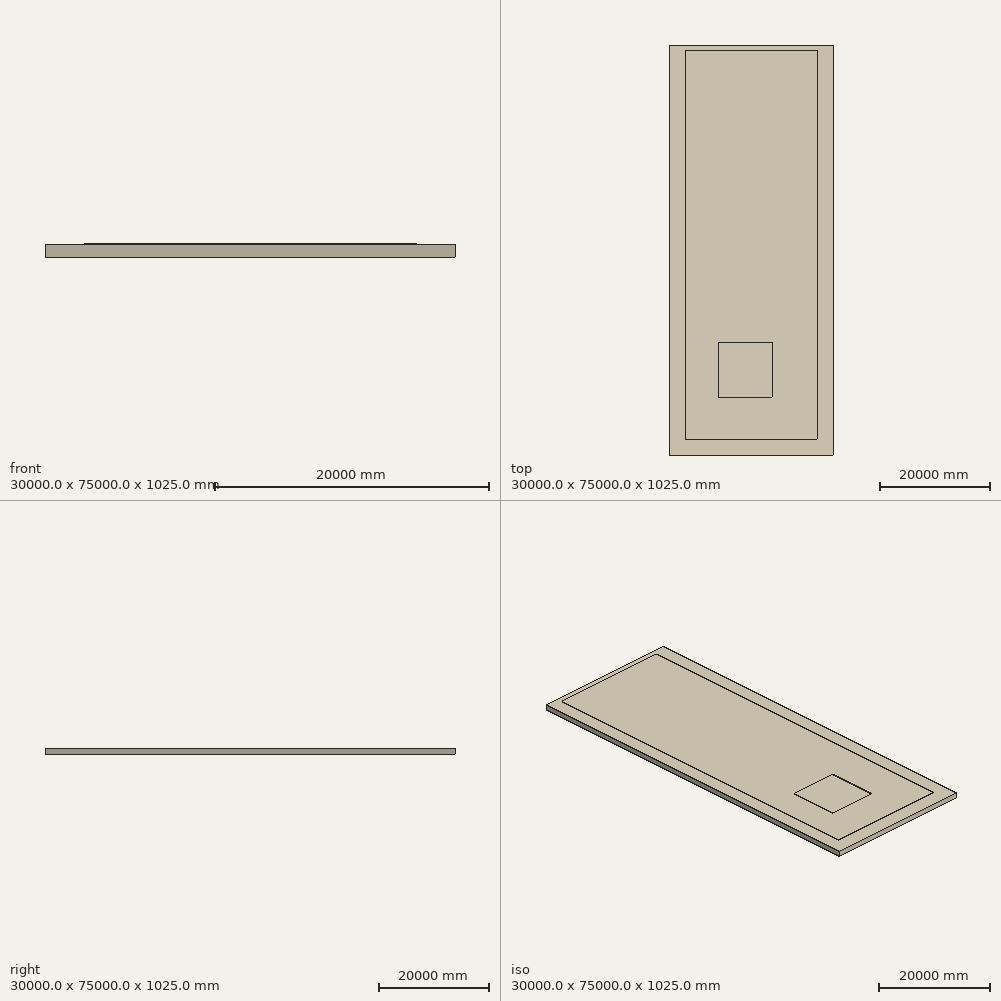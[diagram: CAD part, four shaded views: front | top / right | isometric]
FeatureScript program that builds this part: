
annotation { "Feature Type Name" : "Feature", "Feature Type Description" : "" }
export const myFeature = defineFeature(function(context is Context, id is Id, definition is map)
    precondition{}
    {
        {
            var Q0;
            Q0=qCreatedBy(makeId("Top.planeOp"),FACE);
            var sketch = newSketch(context, id + "F0", { "sketchPlane" : qUnion([Q0])});
            skLineSegment(sketch, "E0.bottom", {"start": v(0, 0) * mm, "end": v(-30000, 0) * mm});
            skLineSegment(sketch, "E0.top", {"start": v(0, 75000) * mm, "end": v(-30000, 75000) * mm});
            skLineSegment(sketch, "E0.left", {"start": v(0, 0) * mm, "end": v(0, 75000) * mm});
            skLineSegment(sketch, "E0.right", {"start": v(-30000, 0) * mm, "end": v(-30000, 75000) * mm});
            skSolve(sketch);
        }
        {
            var Q0;
            Q0 = qSketchRegion(id + "F0", true);
            extrude(context, id + "F1", {"entities" : qUnion([Q0]), "depth" : 1000 * mm});
        }
        {
            var Q0;
            Q0=makeQuery(id+"F1.opExtrude","CAP_FACE",FACE,{"disambiguationData":[OSD([sQuery(id+"F0.wireOp",EDGE,"E0.bottom"),sQuery(id+"F0.wireOp",EDGE,"E0.top"),sQuery(id+"F0.wireOp",EDGE,"E0.left"),sQuery(id+"F0.wireOp",EDGE,"E0.right")])],"isStart":false});
            var sketch = newSketch(context, id + "F2", { "sketchPlane" : qUnion([Q0])});
            skLineSegment(sketch, "E1.bottom", {"start": v(-3000, 3000) * mm, "end": v(-27000, 3000) * mm});
            skLineSegment(sketch, "E1.top", {"start": v(-3000, 74000) * mm, "end": v(-27000, 74000) * mm});
            skLineSegment(sketch, "E1.left", {"start": v(-3000, 3000) * mm, "end": v(-3000, 74000) * mm});
            skLineSegment(sketch, "E1.right", {"start": v(-27000, 3000) * mm, "end": v(-27000, 74000) * mm});
            skLineSegment(sketch, "E2.bottom", {"start": v(-11100, 10600) * mm, "end": v(-21100, 10600) * mm});
            skLineSegment(sketch, "E2.top", {"start": v(-11100, 20600) * mm, "end": v(-21100, 20600) * mm});
            skLineSegment(sketch, "E2.left", {"start": v(-11100, 10600) * mm, "end": v(-11100, 20600) * mm});
            skLineSegment(sketch, "E2.right", {"start": v(-21100, 10600) * mm, "end": v(-21100, 20600) * mm});
            skLineSegment(sketch, "E3", {"start": v(-27000, 3000) * mm, "end": v(-27150, 3000) * mm});
            skLineSegment(sketch, "E4", {"start": v(-27150, 3000) * mm, "end": v(-27150, 74000) * mm});
            skLineSegment(sketch, "E5", {"start": v(-27150, 74000) * mm, "end": v(-27000, 74000) * mm});
            skLineSegment(sketch, "E6", {"start": v(-3000, 74000) * mm, "end": v(-2850, 74000) * mm});
            skLineSegment(sketch, "E7", {"start": v(-2850, 74000) * mm, "end": v(-2850, 3000) * mm});
            skLineSegment(sketch, "E8", {"start": v(-2850, 3000) * mm, "end": v(-3000, 3000) * mm});
            skSolve(sketch);
        }
        {
            var Q0;
            Q0=makeQuery(id+"F2.imprint","IMPRINT",FACE,{"disambiguationData":[TD([[makeQuery(id+"F2.imprint","IMPRINT",EDGE,{"derivedFrom":sQuery(id+"F2.wireOp",EDGE,"E2.bottom")}),-1.0]])]});
            var Q1;
            Q1=sQuery(id+"F2.wireOp",EDGE,"E2.bottom");
            var Q2;
            Q2=sQuery(id+"F2.wireOp",EDGE,"E2.left");
            var Q3;
            Q3=sQuery(id+"F2.wireOp",EDGE,"E2.top");
            var Q4;
            Q4=sQuery(id+"F2.wireOp",EDGE,"E2.right");
            extrude(context, id + "F3", {"entities" : qUnion([Q0]), "operationType" : NewBodyOperationType.REMOVE, "surfaceEntities" : qUnion([Q1, Q2, Q3, Q4]), "oppositeDirection" : true, "depth" : 1 * mm});
        }
        {
            var Q0;
            Q0 = qSketchRegion(id + "F2", true);
            extrude(context, id + "F4", {"entities" : qUnion([Q0]), "operationType" : NewBodyOperationType.ADD, "depth" : 25 * mm});
        }
        {
            var Q0;
            Q0=makeQuery(id+"F1.opExtrude","CAP_FACE",FACE,{"disambiguationData":[OSD([sQuery(id+"F0.wireOp",EDGE,"E0.bottom"),sQuery(id+"F0.wireOp",EDGE,"E0.top"),sQuery(id+"F0.wireOp",EDGE,"E0.left"),sQuery(id+"F0.wireOp",EDGE,"E0.right")])],"isStart":false});
            extrude(context, id + "F5", {"entities" : qUnion([Q0]), "operationType" : NewBodyOperationType.REMOVE, "oppositeDirection" : true, "depth" : 25 * mm});
        }
    });
